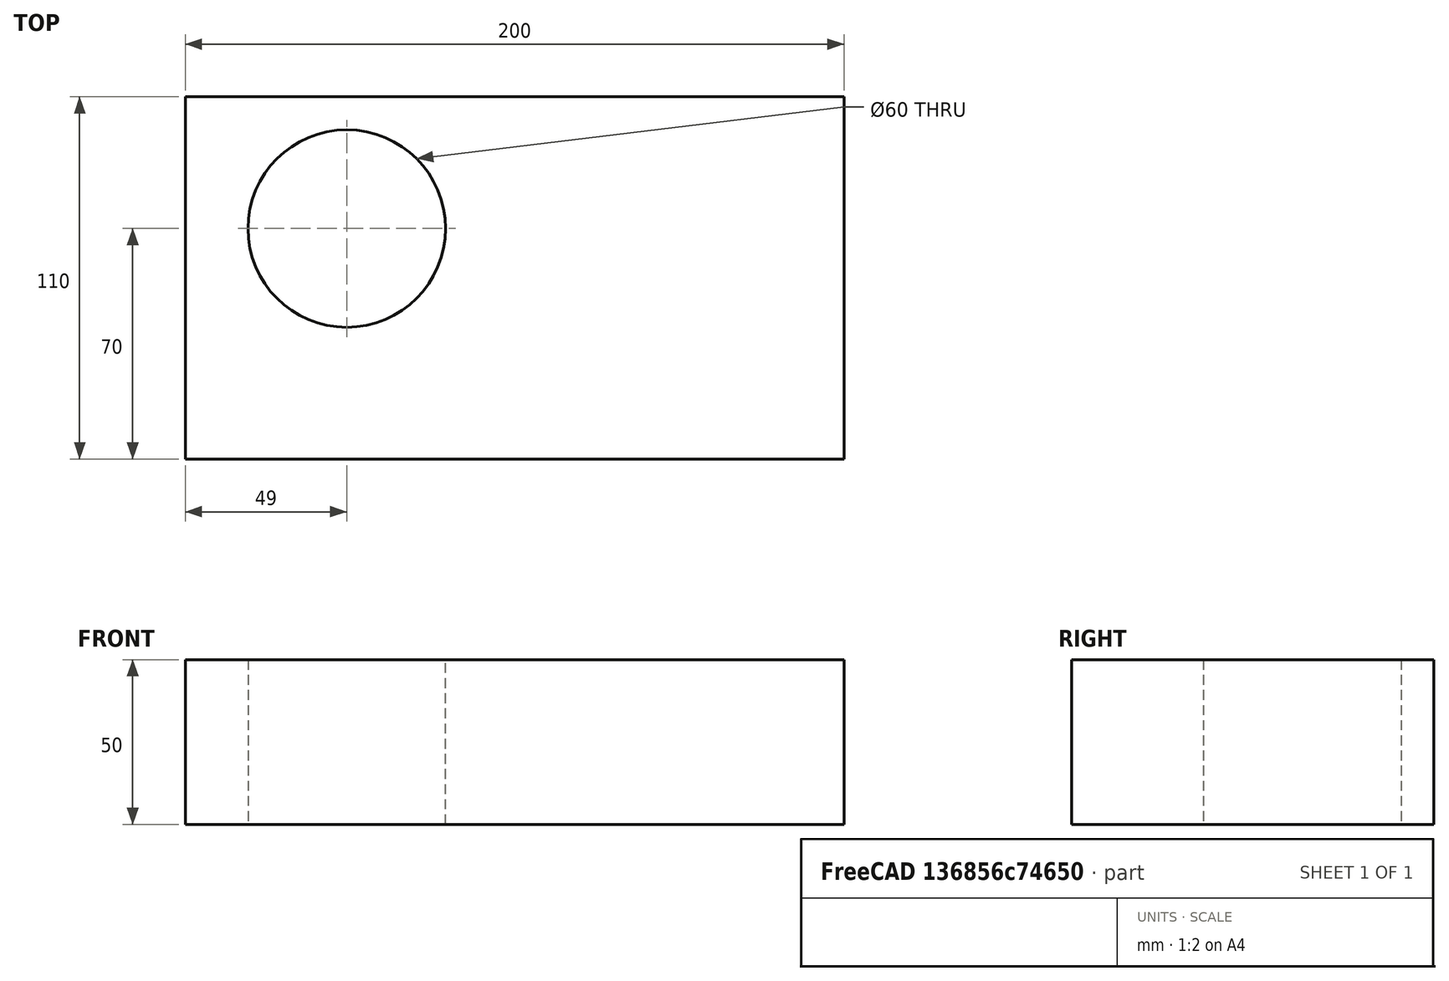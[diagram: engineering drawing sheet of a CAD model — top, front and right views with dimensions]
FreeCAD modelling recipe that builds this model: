
FCSTD DOCUMENT  (FreeCAD 0.18R16131 (Git))
Label: PSU
License: All rights reserved
LicenseURL: http://en.wikipedia.org/wiki/All_rights_reserved
objects: Sketcher::SketchObject×1, PartDesign::Pad×1, PartDesign::Body×1, App::Part×1
note: 4 computed .brp shape members not serialized (recipe doc carries the construction recipe); baked Part::Feature solids carry a one-line shape summary decoded from their .brp

FEATURE [Sketcher::SketchObject] Sketch
  MapMode = 5
  Support = -> [XY_Plane001]
  sketch-geometry (5):
    g0: LineSegment StartX=0 StartY=0 StartZ=0 EndX=200 EndY=0 EndZ=0
    g1: LineSegment StartX=200 StartY=0 StartZ=0 EndX=200 EndY=110 EndZ=0
    g2: LineSegment StartX=200 StartY=110 StartZ=0 EndX=0 EndY=110 EndZ=0
    g3: LineSegment StartX=0 StartY=110 StartZ=0 EndX=0 EndY=0 EndZ=0
    g4: Circle CenterX=49 CenterY=70 CenterZ=0 NormalX=0 NormalY=0 NormalZ=1 AngleXU=0 Radius=30
  constraints (14):
    c: Coincident(g0,g1)
    c: Coincident(g1,g2)
    c: Coincident(g2,g3)
    c: Coincident(g3,g0)
    c: Horizontal(g0)
    c: Horizontal(g2)
    c: Vertical(g1)
    c: Vertical(g3)
    c: Coincident(g0,g-1)
    c: Distance(g3) = 110
    c: Distance(g2) = 200
    c: DistanceX(g-2,g4) = 49
    c: Distance(g4,g2) = 40
    c: Radius(g4) = 30
FEATURE [PartDesign::Pad] Pad
  Length = 50
  Length2 = 100
  Profile = -> Sketch
  Type = 0
FEATURE [PartDesign::Body] Body  label="PSUBody"
  Group = -> [Sketch,Pad]
  Origin = -> Origin001
  Tip = -> Pad
FEATURE [App::Part] Part  label="PSUPart"
  Group = -> [Body]
  Origin = -> Origin
